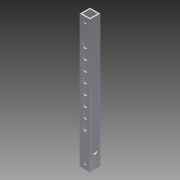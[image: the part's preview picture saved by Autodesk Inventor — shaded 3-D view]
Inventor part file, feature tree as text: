
AUTODESK INVENTOR PART (.ipt)
format: ipt  version: 2015 SP1 (Build 190203100, 203)  size: 145,920 bytes
history: native  units: in
note: dims shown in document units (in); Inventor stores cm internally (conversion verified against a paired STEP export)
features: sketch x5, hole x3, extrude x2, pattern_linear x1
ambient origin geometry x8: Origin, YZ Plane, XZ Plane, XY Plane, X Axis, Y Axis, Z Axis, Center Point
bodies: Solid1 (feature_tree)
feature tree (11):
  extrude  "Extrusion1"  Depth=1.0in
  hole  "Hole1"  [1 undecoded]
  hole  "Hole2"  [1 undecoded]
  hole  "Hole4"  [1 undecoded]
  pattern_linear  "Rectangular Pattern2"  Spacing1=0.5in  [1 undecoded]
  extrude  "Extrusion2"  Depth=1.0in
  sketch  "Sketch1"  dims[d0=1.0in d1=1.0in]
  sketch  "Sketch2"  dims[d2=0.75in d3=0.75in]
  sketch  "Sketch3"  dims[d4=0.125in d5=0.125in]
  sketch  "Sketch5"  dims[d6=13.0in d7=0.0in d8=0.5in]
  sketch  "Sketch6"  dims[d9=0.5in d10=0.5in d11=0.5in d14=0.25in d15=0.75in d16=0.375in d17=0.25in d18=0.5635in d19=1.0in d20=0.8108in d21=0.5in d22=1.5in d23=0.375in d24=0.75in d25=0.375in d26=0.25in d27=0.5635in d28=1.0in d29=0.8108in d42=0.5in d43=3.5in d44=0.5in d45=0.75in d46=0.375in d47=0.25in d48=0.5635in d49=1.0in d50=0.8108in d51=3.1496in d53=1.0in d54=0.5in d55=0.5in d56=0.0in]
note: 4 required parameter values undecoded (feature->parameter linkage not recoverable at this tier; creation-order binding heuristic only, values carry confidence <= 0.55)
